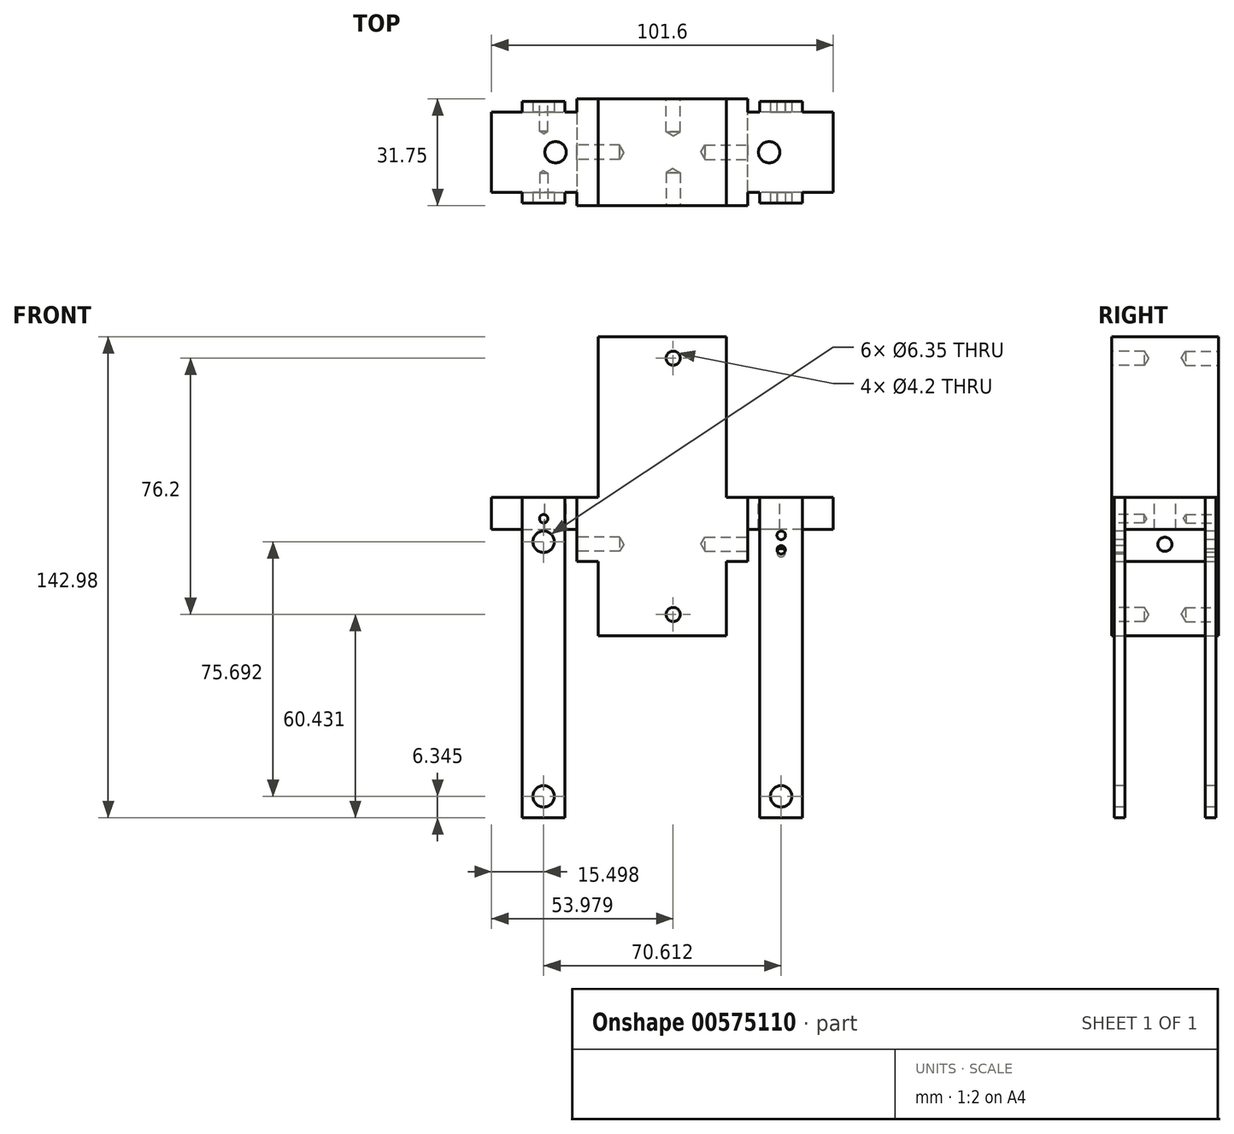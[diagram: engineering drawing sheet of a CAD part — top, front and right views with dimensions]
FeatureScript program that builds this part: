
annotation { "Feature Type Name" : "Feature", "Feature Type Description" : "" }
export const myFeature = defineFeature(function(context is Context, id is Id, definition is map)
    precondition{}
    {
        {
            var Q0;
            Q0=qCreatedBy(makeId("Front.planeOp"),FACE);
            var sketch = newSketch(context, id + "F0", { "sketchPlane" : qUnion([Q0])});
            skLineSegment(sketch, "E0.bottom", {"start": v(-18.07, 30.57) * mm, "end": v(20.03, 30.57) * mm});
            skLineSegment(sketch, "E0.top", {"start": v(-18.07, -58.33) * mm, "end": v(20.03, -58.33) * mm});
            skLineSegment(sketch, "E0.left", {"start": v(-18.07, 30.57) * mm, "end": v(-18.07, -58.33) * mm});
            skLineSegment(sketch, "E0.right", {"start": v(20.03, 30.57) * mm, "end": v(20.03, -58.33) * mm});
            skSolve(sketch);
        }
        {
            var Q0;
            Q0=makeQuery(id+"F0.imprint","IMPRINT",FACE,{"disambiguationData":[TD([[makeQuery(id+"F0.imprint","IMPRINT",EDGE,{"derivedFrom":sQuery(id+"F0.wireOp",EDGE,"E0.bottom")}),-1.0]])]});
            extrude(context, id + "F1", {"entities" : qUnion([Q0]), "depth" : 31.75 * mm, "offsetDistance" : 25.4 * mm});
        }
        {
            var Q0;
            Q0=makeQuery(id+"F1.opExtrude","CAP_FACE",FACE,{"disambiguationData":[OSD([sQuery(id+"F0.wireOp",EDGE,"E0.bottom"),sQuery(id+"F0.wireOp",EDGE,"E0.top"),sQuery(id+"F0.wireOp",EDGE,"E0.left"),sQuery(id+"F0.wireOp",EDGE,"E0.right")])],"isStart":true});
            var sketch = newSketch(context, id + "F2", { "sketchPlane" : qUnion([Q0])});
            skCircle(sketch, "E1", {"center": v(-4.16, 24.22) * mm, "radius": 3.18 * mm});
            skCircle(sketch, "E2", {"center": v(-4.16, -51.98) * mm, "radius": 3.18 * mm});
            skSolve(sketch);
        }
        {
            var Q0;
            Q0=makeQuery(id+"F1.opExtrude","CAP_FACE",FACE,{"disambiguationData":[OSD([sQuery(id+"F0.wireOp",EDGE,"E0.bottom"),sQuery(id+"F0.wireOp",EDGE,"E0.top"),sQuery(id+"F0.wireOp",EDGE,"E0.left"),sQuery(id+"F0.wireOp",EDGE,"E0.right")])],"isStart":false});
            var sketch = newSketch(context, id + "F3", { "sketchPlane" : qUnion([Q0])});
            skCircle(sketch, "E3", {"center": v(4.16, 24.22) * mm, "radius": 3.17 * mm});
            skCircle(sketch, "E4", {"center": v(4.16, -51.98) * mm, "radius": 3.18 * mm});
            skSolve(sketch);
        }
        {
            var Q0;
            Q0=sQuery(id+"F3.wireOp",VERTEX,"E3.center");
            var Q1;
            Q1=sQuery(id+"F3.wireOp",VERTEX,"E4.center");
            var Q2;
            Q2=sQuery(id+"F2.wireOp",VERTEX,"E1.center");
            var Q3;
            Q3=sQuery(id+"F2.wireOp",VERTEX,"E2.center");
            var Q4;
            Q4=makeQuery(id+"F1.opExtrude","SWEPT_BODY",BODY,{"disambiguationData":[OSD([sQuery(id+"F0.wireOp",EDGE,"E0.bottom"),sQuery(id+"F0.wireOp",EDGE,"E0.top"),sQuery(id+"F0.wireOp",EDGE,"E0.left"),sQuery(id+"F0.wireOp",EDGE,"E0.right")])]});
            hole(context, id + "F4", {"style" : HoleStyle.SIMPLE, "endStyle" : HoleEndStyle.BLIND, "standardTappedOrClearance" : lookupTablePath({ "standard" : "ISO", "engagement" : "75%", "pitch" : "0.8 mm", "size" : "M5", "type" : "Tapped" }), "standardBlindInLast" : lookupTablePath({ "standard" : "ISO", "engagement" : "75%", "pitch" : "0.8 mm", "size" : "M5", "type" : "Tapped" }), "holeDiameter" : 4.2 * mm, "showTappedDepth" : true, "holeDepth" : 9.8 * mm, "isTappedThrough" : true, "tappedDepth" : 7.4 * mm, "tapClearance" : 3, "locations" : qUnion([Q0, Q1, Q2, Q3]), "scope" : qUnion([Q4]), "majorDiameter" : 5 * mm});
        }
        {
            var Q0;
            Q0=makeQuery(id+"F1.opExtrude","SWEPT_FACE",FACE,{"disambiguationData":[OSD([sQuery(id+"F0.wireOp",EDGE,"E0.left")])]});
            var sketch = newSketch(context, id + "F5", { "sketchPlane" : qUnion([Q0])});
            skLineSegment(sketch, "E5.bottom", {"start": v(0, -17.16) * mm, "end": v(31.75, -17.16) * mm});
            skLineSegment(sketch, "E5.top", {"start": v(0, -36.21) * mm, "end": v(31.75, -36.21) * mm});
            skLineSegment(sketch, "E5.left", {"start": v(0, -17.16) * mm, "end": v(0, -36.21) * mm});
            skLineSegment(sketch, "E5.right", {"start": v(31.75, -17.16) * mm, "end": v(31.75, -36.21) * mm});
            skSolve(sketch);
        }
        {
            var Q0;
            Q0=makeQuery(id+"F5.imprint","IMPRINT",FACE,{"disambiguationData":[TD([[makeQuery(id+"F5.imprint","IMPRINT",EDGE,{"derivedFrom":sQuery(id+"F5.wireOp",EDGE,"E5.bottom")}),-1.0]])]});
            extrude(context, id + "F6", {"entities" : qUnion([Q0]), "operationType" : NewBodyOperationType.ADD, "depth" : 6.35 * mm, "offsetDistance" : 25.4 * mm});
        }
        {
            var Q0;
            Q0=makeQuery(id+"F6.opExtrude","CAP_FACE",FACE,{"disambiguationData":[OSD([sQuery(id+"F5.wireOp",EDGE,"E5.bottom"),sQuery(id+"F5.wireOp",EDGE,"E5.top"),sQuery(id+"F5.wireOp",EDGE,"E5.left"),sQuery(id+"F5.wireOp",EDGE,"E5.right")])],"isStart":false});
            var sketch = newSketch(context, id + "F7", { "sketchPlane" : qUnion([Q0])});
            skPoint(sketch, "E6.oppositeSnap0", {"position": v(31.75, -26.69) * mm});
            skLineSegment(sketch, "E6.bottom", {"start": v(3.94, -17.16) * mm, "end": v(27.81, -17.16) * mm});
            skLineSegment(sketch, "E6.top", {"start": v(3.94, -26.69) * mm, "end": v(27.81, -26.69) * mm});
            skLineSegment(sketch, "E6.left", {"start": v(3.94, -17.16) * mm, "end": v(3.94, -26.69) * mm});
            skLineSegment(sketch, "E6.right", {"start": v(27.81, -17.16) * mm, "end": v(27.81, -26.69) * mm});
            skSolve(sketch);
        }
        {
            var Q0;
            Q0=makeQuery(id+"F7.imprint","IMPRINT",FACE,{"disambiguationData":[TD([[makeQuery(id+"F7.imprint","IMPRINT",EDGE,{"derivedFrom":sQuery(id+"F7.wireOp",EDGE,"E6.bottom")}),-1.0]])]});
            extrude(context, id + "F8", {"entities" : qUnion([Q0]), "operationType" : NewBodyOperationType.ADD, "depth" : 25.4 * mm, "offsetDistance" : 25.4 * mm});
        }
        {
            var Q0;
            Q0=makeQuery(id+"F6.opExtrude","CAP_FACE",FACE,{"disambiguationData":[OSD([sQuery(id+"F5.wireOp",EDGE,"E5.bottom"),sQuery(id+"F5.wireOp",EDGE,"E5.top"),sQuery(id+"F5.wireOp",EDGE,"E5.left"),sQuery(id+"F5.wireOp",EDGE,"E5.right")])],"isStart":false});
            var sketch = newSketch(context, id + "F9", { "sketchPlane" : qUnion([Q0])});
            skCircle(sketch, "E7", {"center": v(15.88, -31.13) * mm, "radius": 1.7 * mm});
            skPoint(sketch, "E7.centerSnap0", {"position": v(15.88, -36.21) * mm});
            skSolve(sketch);
        }
        {
            var Q0;
            Q0=sQuery(id+"F9.wireOp",VERTEX,"E7.center");
            var Q1;
            Q1=makeQuery(id+"F1.opExtrude","SWEPT_BODY",BODY,{"disambiguationData":[OSD([sQuery(id+"F0.wireOp",EDGE,"E0.bottom"),sQuery(id+"F0.wireOp",EDGE,"E0.top"),sQuery(id+"F0.wireOp",EDGE,"E0.left"),sQuery(id+"F0.wireOp",EDGE,"E0.right")])]});
            hole(context, id + "F10", {"style" : HoleStyle.SIMPLE, "endStyle" : HoleEndStyle.BLIND, "standardTappedOrClearance" : lookupTablePath({ "standard" : "ISO", "engagement" : "75%", "pitch" : "0.8 mm", "size" : "M5", "type" : "Tapped" }), "standardBlindInLast" : lookupTablePath({ "standard" : "ISO", "engagement" : "75%", "pitch" : "0.8 mm", "size" : "M5", "type" : "Tapped" }), "holeDiameter" : 4.2 * mm, "showTappedDepth" : true, "holeDepth" : 12.7 * mm, "isTappedThrough" : true, "tappedDepth" : 10.3 * mm, "tapClearance" : 3, "locations" : qUnion([Q0]), "scope" : qUnion([Q1]), "majorDiameter" : 5 * mm});
        }
        {
            var Q0;
            Q0=makeQuery(id+"F1.opExtrude","SWEPT_FACE",FACE,{"disambiguationData":[OSD([sQuery(id+"F0.wireOp",EDGE,"E0.right")])]});
            var sketch = newSketch(context, id + "F11", { "sketchPlane" : qUnion([Q0])});
            skLineSegment(sketch, "E8.bottom", {"start": v(-31.75, -17.16) * mm, "end": v(0, -17.16) * mm});
            skLineSegment(sketch, "E8.top", {"start": v(-31.75, -36.2) * mm, "end": v(0, -36.2) * mm});
            skLineSegment(sketch, "E8.left", {"start": v(-31.75, -17.16) * mm, "end": v(-31.75, -36.2) * mm});
            skLineSegment(sketch, "E8.right", {"start": v(0, -17.16) * mm, "end": v(0, -36.2) * mm});
            skSolve(sketch);
        }
        {
            var Q0;
            Q0=makeQuery(id+"F11.imprint","IMPRINT",FACE,{"disambiguationData":[TD([[makeQuery(id+"F11.imprint","IMPRINT",EDGE,{"derivedFrom":sQuery(id+"F11.wireOp",EDGE,"E8.bottom")}),-1.0]])]});
            extrude(context, id + "F12", {"entities" : qUnion([Q0]), "operationType" : NewBodyOperationType.ADD, "depth" : 6.35 * mm, "offsetDistance" : 25.4 * mm});
        }
        {
            var Q0;
            Q0=makeQuery(id+"F12.opExtrude","CAP_FACE",FACE,{"disambiguationData":[OSD([sQuery(id+"F11.wireOp",EDGE,"E8.bottom"),sQuery(id+"F11.wireOp",EDGE,"E8.top"),sQuery(id+"F11.wireOp",EDGE,"E8.left"),sQuery(id+"F11.wireOp",EDGE,"E8.right")])],"isStart":false});
            var sketch = newSketch(context, id + "F13", { "sketchPlane" : qUnion([Q0])});
            skLineSegment(sketch, "E9.bottom", {"start": v(-27.81, -17.16) * mm, "end": v(-3.94, -17.16) * mm});
            skLineSegment(sketch, "E9.top", {"start": v(-27.81, -26.68) * mm, "end": v(-3.94, -26.68) * mm});
            skLineSegment(sketch, "E9.left", {"start": v(-27.81, -17.16) * mm, "end": v(-27.81, -26.68) * mm});
            skLineSegment(sketch, "E9.right", {"start": v(-3.94, -17.16) * mm, "end": v(-3.94, -26.68) * mm});
            skSolve(sketch);
        }
        {
            var Q0;
            Q0=makeQuery(id+"F13.imprint","IMPRINT",FACE,{"disambiguationData":[TD([[makeQuery(id+"F13.imprint","IMPRINT",EDGE,{"derivedFrom":sQuery(id+"F13.wireOp",EDGE,"E9.bottom")}),-1.0]])]});
            extrude(context, id + "F14", {"entities" : qUnion([Q0]), "operationType" : NewBodyOperationType.ADD, "depth" : 25.4 * mm, "offsetDistance" : 25.4 * mm});
        }
        {
            var Q0;
            Q0=makeQuery(id+"F12.opExtrude","CAP_FACE",FACE,{"disambiguationData":[OSD([sQuery(id+"F11.wireOp",EDGE,"E8.bottom"),sQuery(id+"F11.wireOp",EDGE,"E8.top"),sQuery(id+"F11.wireOp",EDGE,"E8.left"),sQuery(id+"F11.wireOp",EDGE,"E8.right")])],"isStart":false});
            var sketch = newSketch(context, id + "F15", { "sketchPlane" : qUnion([Q0])});
            skCircle(sketch, "E10", {"center": v(-15.88, -31.13) * mm, "radius": 2.32 * mm});
            skPoint(sketch, "E10.centerSnap0", {"position": v(-15.88, -36.2) * mm});
            skPoint(sketch, "E10.centerSnap1", {"position": v(0, -31.13) * mm});
            skSolve(sketch);
        }
        {
            var Q0;
            Q0=sQuery(id+"F15.wireOp",VERTEX,"E10.center");
            var Q1;
            Q1=makeQuery(id+"F1.opExtrude","SWEPT_BODY",BODY,{"disambiguationData":[OSD([sQuery(id+"F0.wireOp",EDGE,"E0.bottom"),sQuery(id+"F0.wireOp",EDGE,"E0.top"),sQuery(id+"F0.wireOp",EDGE,"E0.left"),sQuery(id+"F0.wireOp",EDGE,"E0.right")])]});
            hole(context, id + "F16", {"style" : HoleStyle.SIMPLE, "endStyle" : HoleEndStyle.BLIND, "standardTappedOrClearance" : lookupTablePath({ "standard" : "ISO", "engagement" : "75%", "pitch" : "0.8 mm", "size" : "M5", "type" : "Tapped" }), "standardBlindInLast" : lookupTablePath({ "standard" : "ISO", "engagement" : "75%", "pitch" : "0.8 mm", "size" : "M5", "type" : "Tapped" }), "holeDiameter" : 4.2 * mm, "showTappedDepth" : true, "holeDepth" : 12.7 * mm, "isTappedThrough" : true, "tappedDepth" : 10.3 * mm, "tapClearance" : 3, "locations" : qUnion([Q0]), "scope" : qUnion([Q1]), "majorDiameter" : 5 * mm});
        }
        {
            var Q0;
            Q0=makeQuery(id+"FRw7JYwWpl1bUgJ_1.boolean.opBoolean","MERGE",FACE,{"derivedFrom":[makeQuery(id+"F12.opExtrude","SWEPT_FACE",FACE,{"disambiguationData":[OSD([sQuery(id+"F11.wireOp",EDGE,"E8.bottom")])]}),makeQuery(id+"FRw7JYwWpl1bUgJ_1.opExtrude","SWEPT_FACE",FACE,{"disambiguationData":[OSD([sQuery(id+"FpIKi7nY0J48hYQ_1.wireOp",EDGE,"1nuKoggT-wq3I-2P69-orzM-hoL9m4IdKjib.bottom")])]})]});
            var sketch = newSketch(context, id + "F17", { "sketchPlane" : qUnion([Q0])});
            skCircle(sketch, "E11", {"center": v(32.73, -15.88) * mm, "radius": 3.17 * mm});
            skCircle(sketch, "E12", {"center": v(-30.77, -15.88) * mm, "radius": 3.18 * mm});
            skSolve(sketch);
        }
        {
            var Q0;
            Q0=makeQuery(id+"F17.imprint","IMPRINT",FACE,{"disambiguationData":[TD([[makeQuery(id+"F17.imprint","IMPRINT",EDGE,{"derivedFrom":sQuery(id+"F17.wireOp",EDGE,"E11")}),1.0]])]});
            var Q1;
            Q1=makeQuery(id+"F17.imprint","IMPRINT",FACE,{"disambiguationData":[TD([[makeQuery(id+"F17.imprint","IMPRINT",EDGE,{"derivedFrom":sQuery(id+"F17.wireOp",EDGE,"E12")}),1.0]])]});
            extrude(context, id + "F18", {"entities" : qUnion([Q0, Q1]), "operationType" : NewBodyOperationType.REMOVE, "endBound" : BoundingType.UP_TO_NEXT, "oppositeDirection" : true, "depth" : 25.4 * mm, "offsetDistance" : 25.4 * mm});
        }
        {
            var Q0;
            Q0=makeQuery(id+"F14.opExtrude","SWEPT_FACE",FACE,{"disambiguationData":[OSD([sQuery(id+"F13.wireOp",EDGE,"E9.right")])]});
            var sketch = newSketch(context, id + "F19", { "sketchPlane" : qUnion([Q0])});
            skLineSegment(sketch, "E13.bottom", {"start": v(-42.64, -17.16) * mm, "end": v(-29.94, -17.16) * mm});
            skLineSegment(sketch, "E13.top", {"start": v(-42.64, -112.4) * mm, "end": v(-29.94, -112.4) * mm});
            skLineSegment(sketch, "E13.left", {"start": v(-42.64, -17.16) * mm, "end": v(-42.64, -112.4) * mm});
            skLineSegment(sketch, "E13.right", {"start": v(-29.94, -17.16) * mm, "end": v(-29.94, -112.4) * mm});
            skSolve(sketch);
        }
        {
            var Q0;
            {var subQ0=sQuery(id+"F19.wireOp",EDGE,"E13.bottom");Q0=makeQuery(id+"F19.imprint","IMPRINT",FACE,{"disambiguationData":[TD([[makeQuery(id+"F19.imprint","IMPRINT",EDGE,{"derivedFrom":subQ0}),-1.0]])]});}
            var Q1;
            {var subQ0=sQuery(id+"F19.wireOp",EDGE,"E13.top");Q1=makeQuery(id+"F19.imprint","IMPRINT",FACE,{"disambiguationData":[TD([[makeQuery(id+"F19.imprint","IMPRINT",EDGE,{"derivedFrom":subQ0}),1.0]])]});}
            extrude(context, id + "F20", {"entities" : qUnion([Q0, Q1]), "operationType" : NewBodyOperationType.ADD, "depth" : 3.17 * mm, "offsetDistance" : 25.4 * mm});
        }
        {
            var Q0;
            Q0=makeQuery(id+"F20.opExtrude","CAP_FACE",FACE,{"disambiguationData":[OSD([sQuery(id+"F19.wireOp",EDGE,"E13.bottom"),sQuery(id+"F19.wireOp",EDGE,"E13.top"),sQuery(id+"F19.wireOp",EDGE,"E13.left"),sQuery(id+"F19.wireOp",EDGE,"E13.right")])],"isStart":false});
            var sketch = newSketch(context, id + "F21", { "sketchPlane" : qUnion([Q0])});
            skCircle(sketch, "E14", {"center": v(-36.29, -33.6) * mm, "radius": 13.74 * mm});
            skPoint(sketch, "E14.centerSnap0", {"position": v(-36.29, -17.16) * mm});
            skSolve(sketch);
        }
        {
            var Q0;
            Q0=sQuery(id+"F21.wireOp",VERTEX,"E14.center");
            var Q1;
            Q1=makeQuery(id+"F1.opExtrude","SWEPT_BODY",BODY,{"disambiguationData":[OSD([sQuery(id+"F0.wireOp",EDGE,"E0.bottom"),sQuery(id+"F0.wireOp",EDGE,"E0.top"),sQuery(id+"F0.wireOp",EDGE,"E0.left"),sQuery(id+"F0.wireOp",EDGE,"E0.right")])]});
            hole(context, id + "F22", {"style" : HoleStyle.SIMPLE, "endStyle" : HoleEndStyle.BLIND, "standardTappedOrClearance" : lookupTablePath({ "standard" : "ISO", "engagement" : "75%", "pitch" : "0.5 mm", "size" : "M3", "type" : "Tapped" }), "standardBlindInLast" : lookupTablePath({ "standard" : "ISO", "engagement" : "75%", "pitch" : "0.5 mm", "size" : "M3", "type" : "Tapped" }), "holeDiameter" : 2.5 * mm, "showTappedDepth" : true, "holeDepth" : 8.9 * mm, "isTappedThrough" : true, "tappedDepth" : 7.4 * mm, "tapClearance" : 3, "locations" : qUnion([Q0]), "scope" : qUnion([Q1]), "majorDiameter" : 3 * mm});
        }
        {
            var Q0;
            Q0=makeQuery(id+"F14.opExtrude","SWEPT_FACE",FACE,{"disambiguationData":[OSD([sQuery(id+"F13.wireOp",EDGE,"E9.left")])]});
            var sketch = newSketch(context, id + "F23", { "sketchPlane" : qUnion([Q0])});
            skLineSegment(sketch, "E15.bottom", {"start": v(29.94, -17.16) * mm, "end": v(42.64, -17.16) * mm});
            skLineSegment(sketch, "E15.top", {"start": v(29.94, -112.4) * mm, "end": v(42.64, -112.4) * mm});
            skLineSegment(sketch, "E15.left", {"start": v(29.94, -17.16) * mm, "end": v(29.94, -112.4) * mm});
            skLineSegment(sketch, "E15.right", {"start": v(42.64, -17.16) * mm, "end": v(42.64, -112.4) * mm});
            skSolve(sketch);
        }
        {
            var Q0;
            {var subQ0=sQuery(id+"F23.wireOp",EDGE,"E15.bottom");Q0=makeQuery(id+"F23.imprint","IMPRINT",FACE,{"disambiguationData":[TD([[makeQuery(id+"F23.imprint","IMPRINT",EDGE,{"derivedFrom":subQ0}),1.0]])]});}
            var Q1;
            {var subQ0=sQuery(id+"F23.wireOp",EDGE,"E15.top");Q1=makeQuery(id+"F23.imprint","IMPRINT",FACE,{"disambiguationData":[TD([[makeQuery(id+"F23.imprint","IMPRINT",EDGE,{"derivedFrom":subQ0}),1.0]])]});}
            extrude(context, id + "F24", {"entities" : qUnion([Q0, Q1]), "operationType" : NewBodyOperationType.ADD, "depth" : 3.17 * mm, "offsetDistance" : 25.4 * mm});
        }
        {
            var Q0;
            Q0=makeQuery(id+"F24.opExtrude","CAP_FACE",FACE,{"disambiguationData":[OSD([sQuery(id+"F23.wireOp",EDGE,"E15.bottom"),sQuery(id+"F23.wireOp",EDGE,"E15.top"),sQuery(id+"F23.wireOp",EDGE,"E15.left"),sQuery(id+"F23.wireOp",EDGE,"E15.right")])],"isStart":false});
            var sketch = newSketch(context, id + "F25", { "sketchPlane" : qUnion([Q0])});
            skCircle(sketch, "E16", {"center": v(36.29, -32.76) * mm, "radius": 12.89 * mm});
            skPoint(sketch, "E16.centerSnap0", {"position": v(36.29, -17.16) * mm});
            skSolve(sketch);
        }
        {
            var Q0;
            Q0=sQuery(id+"F25.wireOp",VERTEX,"E16.center");
            var Q1;
            Q1=makeQuery(id+"F1.opExtrude","SWEPT_BODY",BODY,{"disambiguationData":[OSD([sQuery(id+"F0.wireOp",EDGE,"E0.bottom"),sQuery(id+"F0.wireOp",EDGE,"E0.top"),sQuery(id+"F0.wireOp",EDGE,"E0.left"),sQuery(id+"F0.wireOp",EDGE,"E0.right")])]});
            hole(context, id + "F26", {"style" : HoleStyle.SIMPLE, "endStyle" : HoleEndStyle.BLIND, "standardTappedOrClearance" : lookupTablePath({ "standard" : "ISO", "engagement" : "75%", "pitch" : "0.5 mm", "size" : "M3", "type" : "Tapped" }), "standardBlindInLast" : lookupTablePath({ "standard" : "ISO", "engagement" : "75%", "pitch" : "0.5 mm", "size" : "M3", "type" : "Tapped" }), "holeDiameter" : 2.5 * mm, "showTappedDepth" : true, "holeDepth" : 8.9 * mm, "isTappedThrough" : true, "tappedDepth" : 7.4 * mm, "tapClearance" : 3, "locations" : qUnion([Q0]), "scope" : qUnion([Q1]), "majorDiameter" : 3 * mm});
        }
        {
            var Q0;
            Q0=makeQuery(id+"F24.opExtrude","CAP_FACE",FACE,{"disambiguationData":[OSD([sQuery(id+"F23.wireOp",EDGE,"E15.bottom"),sQuery(id+"F23.wireOp",EDGE,"E15.top"),sQuery(id+"F23.wireOp",EDGE,"E15.left"),sQuery(id+"F23.wireOp",EDGE,"E15.right")])],"isStart":false});
            var sketch = newSketch(context, id + "F27", { "sketchPlane" : qUnion([Q0])});
            skCircle(sketch, "E17", {"center": v(36.29, -28.46) * mm, "radius": 1.27 * mm});
            skPoint(sketch, "E17.centerSnap0", {"position": v(36.29, -17.16) * mm});
            skCircle(sketch, "E18", {"center": v(36.29, -106.06) * mm, "radius": 3.18 * mm});
            skPoint(sketch, "E18.centerSnap0", {"position": v(36.29, -112.4) * mm});
            skSolve(sketch);
        }
        {
            var Q0;
            Q0=makeQuery(id+"F27.imprint","IMPRINT",FACE,{"disambiguationData":[TD([[makeQuery(id+"F27.imprint","IMPRINT",EDGE,{"derivedFrom":sQuery(id+"F27.wireOp",EDGE,"E17")}),1.0]])]});
            var Q1;
            Q1=makeQuery(id+"F27.imprint","IMPRINT",FACE,{"disambiguationData":[TD([[makeQuery(id+"F27.imprint","IMPRINT",EDGE,{"derivedFrom":sQuery(id+"F27.wireOp",EDGE,"E18")}),1.0]])]});
            extrude(context, id + "F28", {"entities" : qUnion([Q0, Q1]), "operationType" : NewBodyOperationType.REMOVE, "endBound" : BoundingType.THROUGH_ALL, "oppositeDirection" : true, "depth" : 25.4 * mm, "offsetDistance" : 25.4 * mm});
        }
        {
            var Q0;
            Q0=makeQuery(id+"F8.opExtrude","SWEPT_FACE",FACE,{"disambiguationData":[OSD([sQuery(id+"F7.wireOp",EDGE,"E6.right")])]});
            var sketch = newSketch(context, id + "F29", { "sketchPlane" : qUnion([Q0])});
            skLineSegment(sketch, "E19.bottom", {"start": v(-40.67, -17.16) * mm, "end": v(-27.97, -17.16) * mm});
            skLineSegment(sketch, "E19.top", {"start": v(-40.67, -112.41) * mm, "end": v(-27.97, -112.41) * mm});
            skLineSegment(sketch, "E19.left", {"start": v(-40.67, -17.16) * mm, "end": v(-40.67, -112.41) * mm});
            skLineSegment(sketch, "E19.right", {"start": v(-27.97, -17.16) * mm, "end": v(-27.97, -112.41) * mm});
            skSolve(sketch);
        }
        {
            var Q0;
            {var subQ0=sQuery(id+"F29.wireOp",EDGE,"E19.top");Q0=makeQuery(id+"F29.imprint","IMPRINT",FACE,{"disambiguationData":[TD([[makeQuery(id+"F29.imprint","IMPRINT",EDGE,{"derivedFrom":subQ0}),1.0]])]});}
            var Q1;
            {var subQ0=sQuery(id+"F29.wireOp",EDGE,"E19.bottom");Q1=makeQuery(id+"F29.imprint","IMPRINT",FACE,{"disambiguationData":[TD([[makeQuery(id+"F29.imprint","IMPRINT",EDGE,{"derivedFrom":subQ0}),-1.0]])]});}
            extrude(context, id + "F30", {"entities" : qUnion([Q0, Q1]), "operationType" : NewBodyOperationType.ADD, "depth" : 3.17 * mm, "offsetDistance" : 25.4 * mm});
        }
        {
            var Q0;
            Q0=makeQuery(id+"F30.opExtrude","CAP_FACE",FACE,{"disambiguationData":[OSD([sQuery(id+"F29.wireOp",EDGE,"E19.bottom"),sQuery(id+"F29.wireOp",EDGE,"E19.top"),sQuery(id+"F29.wireOp",EDGE,"E19.left"),sQuery(id+"F29.wireOp",EDGE,"E19.right")])],"isStart":false});
            var sketch = newSketch(context, id + "F31", { "sketchPlane" : qUnion([Q0])});
            skCircle(sketch, "E20", {"center": v(-34.32, -106.06) * mm, "radius": 3.18 * mm});
            skPoint(sketch, "E20.centerSnap0", {"position": v(-34.32, -112.41) * mm});
            skCircle(sketch, "E21", {"center": v(-34.32, -30.37) * mm, "radius": 3.18 * mm});
            skSolve(sketch);
        }
        {
            var Q0;
            Q0=makeQuery(id+"F8.opExtrude","SWEPT_FACE",FACE,{"disambiguationData":[OSD([sQuery(id+"F7.wireOp",EDGE,"E6.left")])]});
            var sketch = newSketch(context, id + "F32", { "sketchPlane" : qUnion([Q0])});
            skLineSegment(sketch, "E22.bottom", {"start": v(27.97, -17.16) * mm, "end": v(40.67, -17.16) * mm});
            skLineSegment(sketch, "E22.top", {"start": v(27.97, -112.41) * mm, "end": v(40.67, -112.41) * mm});
            skLineSegment(sketch, "E22.left", {"start": v(27.97, -17.16) * mm, "end": v(27.97, -112.41) * mm});
            skLineSegment(sketch, "E22.right", {"start": v(40.67, -17.16) * mm, "end": v(40.67, -112.41) * mm});
            skSolve(sketch);
        }
        {
            var Q0;
            {var subQ0=sQuery(id+"F32.wireOp",EDGE,"E22.bottom");Q0=makeQuery(id+"F32.imprint","IMPRINT",FACE,{"disambiguationData":[TD([[makeQuery(id+"F32.imprint","IMPRINT",EDGE,{"derivedFrom":subQ0}),1.0]])]});}
            var Q1;
            {var subQ0=sQuery(id+"F32.wireOp",EDGE,"E22.top");Q1=makeQuery(id+"F32.imprint","IMPRINT",FACE,{"disambiguationData":[TD([[makeQuery(id+"F32.imprint","IMPRINT",EDGE,{"derivedFrom":subQ0}),1.0]])]});}
            extrude(context, id + "F33", {"entities" : qUnion([Q0, Q1]), "operationType" : NewBodyOperationType.ADD, "depth" : 3.17 * mm, "offsetDistance" : 25.4 * mm});
        }
        {
            var Q0;
            Q0=makeQuery(id+"F33.opExtrude","CAP_FACE",FACE,{"disambiguationData":[OSD([sQuery(id+"F32.wireOp",EDGE,"E22.bottom"),sQuery(id+"F32.wireOp",EDGE,"E22.top"),sQuery(id+"F32.wireOp",EDGE,"E22.left"),sQuery(id+"F32.wireOp",EDGE,"E22.right")])],"isStart":false});
            var sketch = newSketch(context, id + "F34", { "sketchPlane" : qUnion([Q0])});
            skCircle(sketch, "E23", {"center": v(34.32, -23.51) * mm, "radius": 1.3 * mm});
            skPoint(sketch, "E23.centerSnap0", {"position": v(34.32, -17.16) * mm});
            skSolve(sketch);
        }
        {
            var Q0;
            Q0=sQuery(id+"F34.wireOp",VERTEX,"E23.center");
            var Q1;
            Q1=makeQuery(id+"F1.opExtrude","SWEPT_BODY",BODY,{"disambiguationData":[OSD([sQuery(id+"F0.wireOp",EDGE,"E0.bottom"),sQuery(id+"F0.wireOp",EDGE,"E0.top"),sQuery(id+"F0.wireOp",EDGE,"E0.left"),sQuery(id+"F0.wireOp",EDGE,"E0.right")])]});
            hole(context, id + "F35", {"style" : HoleStyle.SIMPLE, "endStyle" : HoleEndStyle.BLIND, "standardTappedOrClearance" : lookupTablePath({ "standard" : "ISO", "engagement" : "75%", "pitch" : "0.5 mm", "size" : "M3", "type" : "Tapped" }), "standardBlindInLast" : lookupTablePath({ "standard" : "ISO", "engagement" : "75%", "pitch" : "0.5 mm", "size" : "M3", "type" : "Tapped" }), "holeDiameter" : 2.5 * mm, "showTappedDepth" : true, "holeDepth" : 8.9 * mm, "isTappedThrough" : true, "tappedDepth" : 7.4 * mm, "tapClearance" : 3, "locations" : qUnion([Q0]), "scope" : qUnion([Q1]), "majorDiameter" : 3 * mm});
        }
        {
            var Q0;
            Q0=makeQuery(id+"F31.imprint","IMPRINT",FACE,{"disambiguationData":[TD([[makeQuery(id+"F31.imprint","IMPRINT",EDGE,{"derivedFrom":sQuery(id+"F31.wireOp",EDGE,"E21")}),1.0]])]});
            var Q1;
            Q1=makeQuery(id+"F31.imprint","IMPRINT",FACE,{"disambiguationData":[TD([[makeQuery(id+"F31.imprint","IMPRINT",EDGE,{"derivedFrom":sQuery(id+"F31.wireOp",EDGE,"E20")}),1.0]])]});
            extrude(context, id + "F36", {"entities" : qUnion([Q0, Q1]), "operationType" : NewBodyOperationType.REMOVE, "oppositeDirection" : true, "depth" : 127 * mm, "offsetDistance" : 25.4 * mm});
        }
        {
            var Q0;
            Q0=makeQuery(id+"F30.opExtrude","CAP_FACE",FACE,{"disambiguationData":[OSD([sQuery(id+"F29.wireOp",EDGE,"E19.bottom"),sQuery(id+"F29.wireOp",EDGE,"E19.top"),sQuery(id+"F29.wireOp",EDGE,"E19.left"),sQuery(id+"F29.wireOp",EDGE,"E19.right")])],"isStart":false});
            var sketch = newSketch(context, id + "F37", { "sketchPlane" : qUnion([Q0])});
            skCircle(sketch, "E24", {"center": v(-34.32, -23.51) * mm, "radius": 1.59 * mm});
            skSolve(sketch);
        }
        {
            var Q0;
            Q0=sQuery(id+"F37.wireOp",VERTEX,"E24.center");
            var Q1;
            Q1=makeQuery(id+"F1.opExtrude","SWEPT_BODY",BODY,{"disambiguationData":[OSD([sQuery(id+"F0.wireOp",EDGE,"E0.bottom"),sQuery(id+"F0.wireOp",EDGE,"E0.top"),sQuery(id+"F0.wireOp",EDGE,"E0.left"),sQuery(id+"F0.wireOp",EDGE,"E0.right")])]});
            hole(context, id + "F38", {"style" : HoleStyle.SIMPLE, "endStyle" : HoleEndStyle.BLIND, "standardTappedOrClearance" : lookupTablePath({ "standard" : "ISO", "engagement" : "75%", "pitch" : "0.5 mm", "size" : "M3", "type" : "Tapped" }), "standardBlindInLast" : lookupTablePath({ "standard" : "ISO", "engagement" : "75%", "pitch" : "0.5 mm", "size" : "M3", "type" : "Tapped" }), "holeDiameter" : 2.5 * mm, "majorDiameter" : 3 * mm, "showTappedDepth" : true, "holeDepth" : 8.9 * mm, "isTappedThrough" : true, "tappedDepth" : 7.4 * mm, "tapClearance" : 3, "locations" : qUnion([Q0]), "scope" : qUnion([Q1])});
        }
    });
